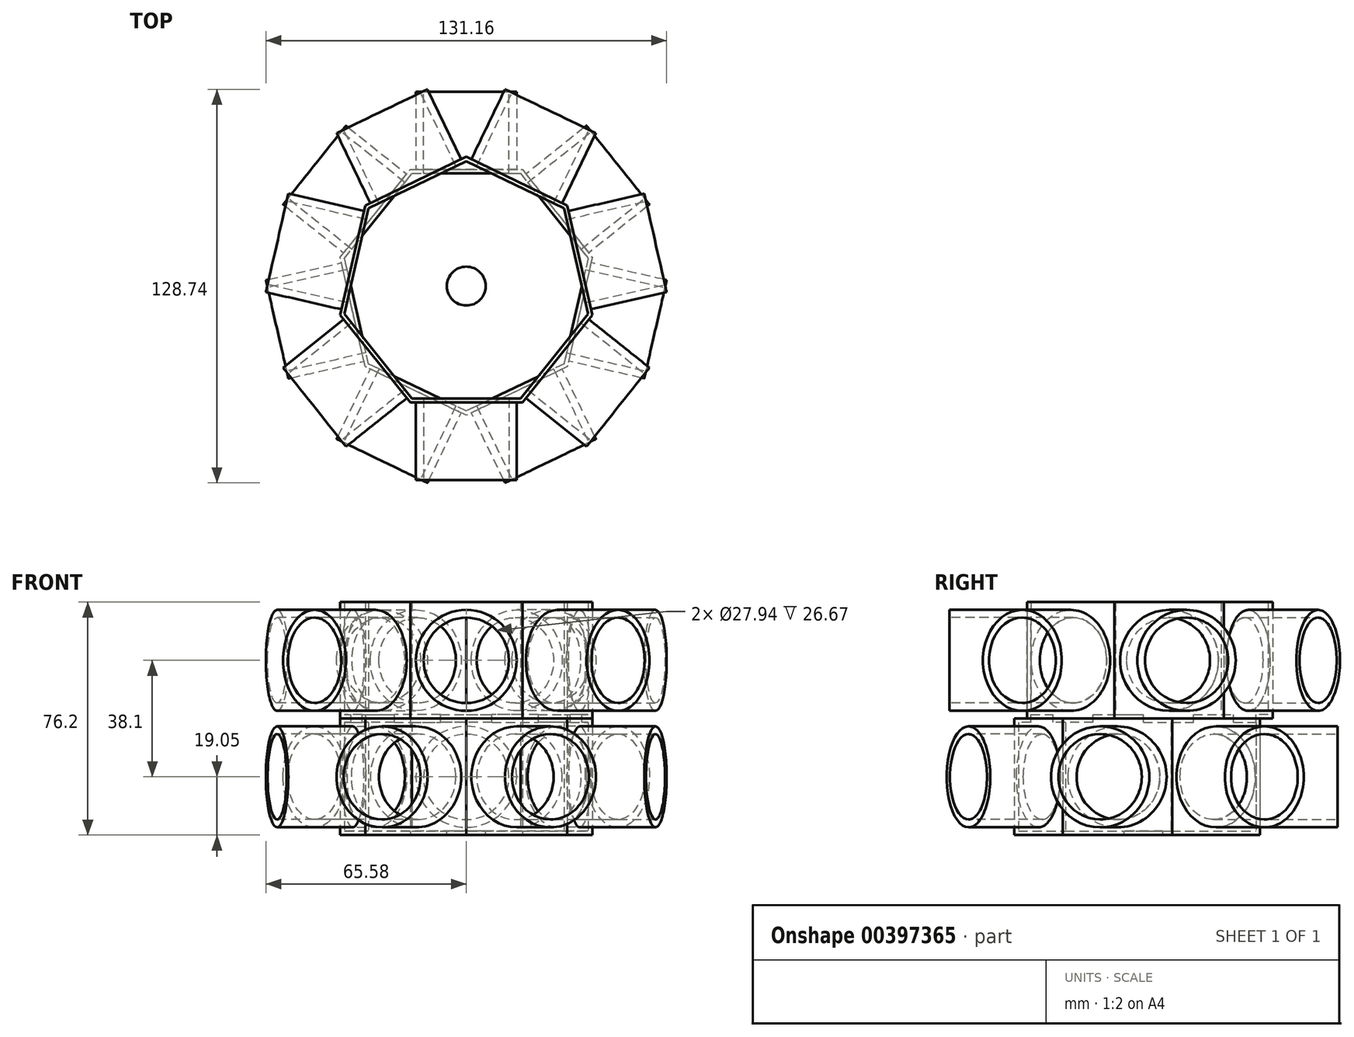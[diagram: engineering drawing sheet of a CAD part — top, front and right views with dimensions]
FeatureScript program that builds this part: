
annotation { "Feature Type Name" : "Feature", "Feature Type Description" : "" }
export const myFeature = defineFeature(function(context is Context, id is Id, definition is map)
    precondition{}
    {
        {
            var Q0;
            Q0=qCreatedBy(makeId("Top.planeOp"),FACE);
            var sketch = newSketch(context, id + "F0", { "sketchPlane" : qUnion([Q0])});
            skCircle(sketch, "E0.cCircle", {"center": v(0, 0) * mm, "radius": 38.1 * mm, "construction": true});
            skLineSegment(sketch, "E0.0", {"start": v(-18.35, 38.1) * mm, "end": v(18.35, 38.1) * mm});
            skLineSegment(sketch, "E0.1", {"start": v(18.35, 38.1) * mm, "end": v(41.23, 9.4) * mm});
            skLineSegment(sketch, "E0.2", {"start": v(41.23, 9.4) * mm, "end": v(33.06, -26.37) * mm});
            skLineSegment(sketch, "E0.3", {"start": v(33.06, -26.37) * mm, "end": v(0, -42.29) * mm});
            skLineSegment(sketch, "E0.4", {"start": v(0, -42.29) * mm, "end": v(-33.06, -26.37) * mm});
            skLineSegment(sketch, "E0.5", {"start": v(-33.06, -26.37) * mm, "end": v(-41.23, 9.4) * mm});
            skLineSegment(sketch, "E0.6", {"start": v(-41.23, 9.4) * mm, "end": v(-18.35, 38.1) * mm});
            skPoint(sketch, "E0.0.midPoint", {"position": v(0, 38.1) * mm});
            skSolve(sketch);
        }
        {
            var Q0;
            Q0=makeQuery(id+"F0.imprint","IMPRINT",FACE,{"disambiguationData":[TD([[makeQuery(id+"F0.imprint","IMPRINT",EDGE,{"derivedFrom":sQuery(id+"F0.wireOp",EDGE,"E0.0")}),-1.0]])]});
            extrude(context, id + "F1", {"entities" : qUnion([Q0]), "depth" : 38.1 * mm});
        }
        {
            var Q0;
            Q0=makeQuery(id+"F1.opExtrude","CAP_FACE",FACE,{"disambiguationData":[OSD([sQuery(id+"F0.wireOp",EDGE,"E0.0"),sQuery(id+"F0.wireOp",EDGE,"E0.1"),sQuery(id+"F0.wireOp",EDGE,"E0.2"),sQuery(id+"F0.wireOp",EDGE,"E0.3"),sQuery(id+"F0.wireOp",EDGE,"E0.4"),sQuery(id+"F0.wireOp",EDGE,"E0.5"),sQuery(id+"F0.wireOp",EDGE,"E0.6")])],"isStart":false});
            var sketch = newSketch(context, id + "F2", { "sketchPlane" : qUnion([Q0])});
            skCircle(sketch, "E1.cCircle", {"center": v(0, 0) * mm, "radius": 38.1 * mm, "construction": true});
            skLineSegment(sketch, "E1.0", {"start": v(0, 42.29) * mm, "end": v(33.06, 26.37) * mm});
            skLineSegment(sketch, "E1.1", {"start": v(33.06, 26.37) * mm, "end": v(41.23, -9.4) * mm});
            skLineSegment(sketch, "E1.2", {"start": v(41.23, -9.4) * mm, "end": v(18.35, -38.1) * mm});
            skLineSegment(sketch, "E1.3", {"start": v(18.35, -38.1) * mm, "end": v(-18.35, -38.1) * mm});
            skLineSegment(sketch, "E1.4", {"start": v(-18.35, -38.1) * mm, "end": v(-41.23, -9.4) * mm});
            skLineSegment(sketch, "E1.5", {"start": v(-41.23, -9.4) * mm, "end": v(-33.06, 26.37) * mm});
            skLineSegment(sketch, "E1.6", {"start": v(-33.06, 26.37) * mm, "end": v(0, 42.29) * mm});
            skPoint(sketch, "E1.0.midPoint", {"position": v(16.53, 34.33) * mm});
            skSolve(sketch);
        }
        {
            var Q0;
            {var subQ0=sQuery(id+"F2.wireOp",EDGE,"E1.6");var subQ1=sQuery(id+"F2.wireOp",EDGE,"E1.5");var subQ2=makeQuery(id+"F2.imprint","INTERSECT",VERTEX,{"derivedFrom":[subQ1,subQ0]});Q0=makeQuery(id+"F2.imprint","IMPRINT",FACE,{"disambiguationData":[TD([[makeQuery(id+"F2.imprint","IMPRINT",EDGE,{"disambiguationData":[TD([[subQ2,1.0]])],"derivedFrom":subQ1}),-1.0]])]});}
            var Q1;
            {var subQ0=sQuery(id+"F2.wireOp",EDGE,"E1.6");var subQ1=sQuery(id+"F2.wireOp",EDGE,"E1.0");var subQ2=makeQuery(id+"F2.imprint","INTERSECT",VERTEX,{"derivedFrom":[subQ1,subQ0]});Q1=makeQuery(id+"F2.imprint","IMPRINT",FACE,{"disambiguationData":[TD([[makeQuery(id+"F2.imprint","IMPRINT",EDGE,{"disambiguationData":[TD([[subQ2,-1.0]])],"derivedFrom":subQ1}),-1.0]])]});}
            var Q2;
            {var subQ0=sQuery(id+"F2.wireOp",EDGE,"E1.1");var subQ1=sQuery(id+"F2.wireOp",EDGE,"E1.0");var subQ2=makeQuery(id+"F2.imprint","INTERSECT",VERTEX,{"derivedFrom":[subQ1,subQ0]});Q2=makeQuery(id+"F2.imprint","IMPRINT",FACE,{"disambiguationData":[TD([[makeQuery(id+"F2.imprint","IMPRINT",EDGE,{"disambiguationData":[TD([[subQ2,1.0]])],"derivedFrom":subQ1}),-1.0]])]});}
            var Q3;
            {var subQ0=sQuery(id+"F2.wireOp",EDGE,"E1.2");var subQ1=sQuery(id+"F2.wireOp",EDGE,"E1.1");var subQ2=makeQuery(id+"F2.imprint","INTERSECT",VERTEX,{"derivedFrom":[subQ1,subQ0]});Q3=makeQuery(id+"F2.imprint","IMPRINT",FACE,{"disambiguationData":[TD([[makeQuery(id+"F2.imprint","IMPRINT",EDGE,{"disambiguationData":[TD([[subQ2,1.0]])],"derivedFrom":subQ1}),-1.0]])]});}
            var Q4;
            {var subQ0=sQuery(id+"F2.wireOp",EDGE,"E1.5");var subQ1=sQuery(id+"F2.wireOp",EDGE,"E1.4");var subQ2=makeQuery(id+"F2.imprint","INTERSECT",VERTEX,{"derivedFrom":[subQ1,subQ0]});Q4=makeQuery(id+"F2.imprint","IMPRINT",FACE,{"disambiguationData":[TD([[makeQuery(id+"F2.imprint","IMPRINT",EDGE,{"disambiguationData":[TD([[subQ2,1.0]])],"derivedFrom":subQ1}),-1.0]])]});}
            var Q5;
            {var subQ0=sQuery(id+"F2.wireOp",EDGE,"E1.4");var subQ1=sQuery(id+"F2.wireOp",EDGE,"E1.3");var subQ2=makeQuery(id+"F2.imprint","INTERSECT",VERTEX,{"derivedFrom":[subQ1,subQ0]});Q5=makeQuery(id+"F2.imprint","IMPRINT",FACE,{"disambiguationData":[TD([[makeQuery(id+"F2.imprint","IMPRINT",EDGE,{"disambiguationData":[TD([[subQ2,1.0]])],"derivedFrom":subQ1}),-1.0]])]});}
            var Q6;
            {var subQ0=sQuery(id+"F2.wireOp",EDGE,"E1.3");var subQ1=sQuery(id+"F2.wireOp",EDGE,"E1.2");var subQ2=makeQuery(id+"F2.imprint","INTERSECT",VERTEX,{"derivedFrom":[subQ1,subQ0]});Q6=makeQuery(id+"F2.imprint","IMPRINT",FACE,{"disambiguationData":[TD([[makeQuery(id+"F2.imprint","IMPRINT",EDGE,{"disambiguationData":[TD([[subQ2,1.0]])],"derivedFrom":subQ1}),-1.0]])]});}
            var Q7;
            {var subQ3=makeQuery(id+"F1.opExtrude","CAP_EDGE",EDGE,{"disambiguationData":[OSD([sQuery(id+"F0.wireOp",EDGE,"E0.0")])],"isStart":false});var subQ13=sQuery(id+"F2.wireOp",EDGE,"E1.0");var subQ14=makeQuery(id+"F2.imprint","INTERSECT",VERTEX,{"derivedFrom":[subQ3,subQ13]});Q7=makeQuery(id+"F2.imprint","IMPRINT",FACE,{"disambiguationData":[TD([[makeQuery(id+"F2.imprint","IMPRINT",EDGE,{"disambiguationData":[TD([[subQ14,-1.0]])],"derivedFrom":subQ13}),-1.0]])]});}
            extrude(context, id + "F3", {"entities" : qUnion([Q0, Q1, Q2, Q3, Q4, Q5, Q6, Q7]), "operationType" : NewBodyOperationType.ADD, "depth" : 38.1 * mm});
        }
        {
            var Q0;
            Q0=makeQuery(id+"F3.opExtrude","CAP_FACE",FACE,{"disambiguationData":[OSD([sQuery(id+"F2.wireOp",EDGE,"E1.0"),sQuery(id+"F2.wireOp",EDGE,"E1.1"),sQuery(id+"F2.wireOp",EDGE,"E1.2"),sQuery(id+"F2.wireOp",EDGE,"E1.3"),sQuery(id+"F2.wireOp",EDGE,"E1.4"),sQuery(id+"F2.wireOp",EDGE,"E1.5"),sQuery(id+"F2.wireOp",EDGE,"E1.6")])],"isStart":false});
            shell(context, id + "F4", {"entities" : qUnion([Q0]), "thickness" : 1.27 * mm});
        }
        {
            var Q0;
            Q0=makeQuery(id+"F1.opExtrude","CAP_FACE",FACE,{"disambiguationData":[OSD([sQuery(id+"F0.wireOp",EDGE,"E0.0"),sQuery(id+"F0.wireOp",EDGE,"E0.1"),sQuery(id+"F0.wireOp",EDGE,"E0.2"),sQuery(id+"F0.wireOp",EDGE,"E0.3"),sQuery(id+"F0.wireOp",EDGE,"E0.4"),sQuery(id+"F0.wireOp",EDGE,"E0.5"),sQuery(id+"F0.wireOp",EDGE,"E0.6")])],"isStart":true});
            var sketch = newSketch(context, id + "F5", { "sketchPlane" : qUnion([Q0])});
            skCircle(sketch, "E2", {"center": v(0, 0) * mm, "radius": 34.93 * mm});
            skSolve(sketch);
        }
        {
            var Q0;
            Q0=sQuery(id+"F5.wireOp",VERTEX,"E2.center");
            var Q1;
            Q1=makeQuery(id+"F1.opExtrude","SWEPT_BODY",BODY,{"disambiguationData":[OSD([sQuery(id+"F0.wireOp",EDGE,"E0.0"),sQuery(id+"F0.wireOp",EDGE,"E0.1"),sQuery(id+"F0.wireOp",EDGE,"E0.2"),sQuery(id+"F0.wireOp",EDGE,"E0.3"),sQuery(id+"F0.wireOp",EDGE,"E0.4"),sQuery(id+"F0.wireOp",EDGE,"E0.5"),sQuery(id+"F0.wireOp",EDGE,"E0.6")])]});
            hole(context, id + "F6", {"style" : HoleStyle.SIMPLE, "endStyle" : HoleEndStyle.THROUGH, "holeDiameter" : 12.7 * mm, "isTappedThrough" : true, "tappedDepth" : 12.7 * mm, "tapClearance" : 3, "startFromSketch" : true, "locations" : qUnion([Q0]), "scope" : qUnion([Q1])});
        }
        {
            var Q0;
            Q0=makeQuery(id+"F1.opExtrude","SWEPT_FACE",FACE,{"disambiguationData":[OSD([sQuery(id+"F0.wireOp",EDGE,"E0.0")])]});
            var sketch = newSketch(context, id + "F7", { "sketchPlane" : qUnion([Q0])});
            skCircle(sketch, "E3", {"center": v(0, 19.05) * mm, "radius": 13.97 * mm});
            skPoint(sketch, "E3.centerSnap0", {"position": v(18.35, 19.05) * mm});
            skCircle(sketch, "E4", {"center": v(0, 19.05) * mm, "radius": 16.51 * mm});
            skSolve(sketch);
        }
        {
            var Q0;
            Q0=makeQuery(id+"F7.imprint","IMPRINT",FACE,{"disambiguationData":[TD([[makeQuery(id+"F7.imprint","IMPRINT",EDGE,{"derivedFrom":sQuery(id+"F7.wireOp",EDGE,"E3")}),1.0]])]});
            extrude(context, id + "F8", {"entities" : qUnion([Q0]), "operationType" : NewBodyOperationType.REMOVE, "oppositeDirection" : true, "depth" : 25.4 * mm});
        }
        {
            var Q0;
            Q0=makeQuery(id+"F1.opExtrude","SWEPT_FACE",FACE,{"disambiguationData":[OSD([sQuery(id+"F0.wireOp",EDGE,"E0.1")])]});
            var sketch = newSketch(context, id + "F9", { "sketchPlane" : qUnion([Q0])});
            skCircle(sketch, "E5", {"center": v(0, 19.05) * mm, "radius": 13.97 * mm});
            skPoint(sketch, "E5.centerSnap0", {"position": v(-18.35, 19.05) * mm});
            skCircle(sketch, "E6", {"center": v(0, 19.05) * mm, "radius": 16.51 * mm});
            skSolve(sketch);
        }
        {
            var Q0;
            Q0=makeQuery(id+"F9.imprint","IMPRINT",FACE,{"disambiguationData":[TD([[makeQuery(id+"F9.imprint","IMPRINT",EDGE,{"derivedFrom":sQuery(id+"F9.wireOp",EDGE,"E5")}),1.0]])]});
            extrude(context, id + "F10", {"entities" : qUnion([Q0]), "operationType" : NewBodyOperationType.REMOVE, "oppositeDirection" : true, "depth" : 25.4 * mm});
        }
        {
            var Q0;
            Q0=makeQuery(id+"F1.opExtrude","SWEPT_FACE",FACE,{"disambiguationData":[OSD([sQuery(id+"F0.wireOp",EDGE,"E0.2")])]});
            var sketch = newSketch(context, id + "F11", { "sketchPlane" : qUnion([Q0])});
            skCircle(sketch, "E7", {"center": v(0, 19.05) * mm, "radius": 13.97 * mm});
            skPoint(sketch, "E7.centerSnap0", {"position": v(-18.35, 19.05) * mm});
            skCircle(sketch, "E8", {"center": v(0, 19.05) * mm, "radius": 16.51 * mm});
            skSolve(sketch);
        }
        {
            var Q0;
            Q0=makeQuery(id+"F11.imprint","IMPRINT",FACE,{"disambiguationData":[TD([[makeQuery(id+"F11.imprint","IMPRINT",EDGE,{"derivedFrom":sQuery(id+"F11.wireOp",EDGE,"E7")}),1.0]])]});
            extrude(context, id + "F12", {"entities" : qUnion([Q0]), "operationType" : NewBodyOperationType.REMOVE, "oppositeDirection" : true, "depth" : 25.4 * mm});
        }
        {
            var Q0;
            Q0=makeQuery(id+"F1.opExtrude","SWEPT_FACE",FACE,{"disambiguationData":[OSD([sQuery(id+"F0.wireOp",EDGE,"E0.3")])]});
            var sketch = newSketch(context, id + "F13", { "sketchPlane" : qUnion([Q0])});
            skCircle(sketch, "E9", {"center": v(0, 19.05) * mm, "radius": 13.97 * mm});
            skPoint(sketch, "E9.centerSnap0", {"position": v(18.35, 19.05) * mm});
            skCircle(sketch, "E10", {"center": v(0, 19.05) * mm, "radius": 16.51 * mm});
            skSolve(sketch);
        }
        {
            var Q0;
            Q0=makeQuery(id+"F13.imprint","IMPRINT",FACE,{"disambiguationData":[TD([[makeQuery(id+"F13.imprint","IMPRINT",EDGE,{"derivedFrom":sQuery(id+"F13.wireOp",EDGE,"E9")}),1.0]])]});
            extrude(context, id + "F14", {"entities" : qUnion([Q0]), "operationType" : NewBodyOperationType.REMOVE, "oppositeDirection" : true, "depth" : 25.4 * mm});
        }
        {
            var Q0;
            Q0=makeQuery(id+"F1.opExtrude","SWEPT_FACE",FACE,{"disambiguationData":[OSD([sQuery(id+"F0.wireOp",EDGE,"E0.5")])]});
            var sketch = newSketch(context, id + "F15", { "sketchPlane" : qUnion([Q0])});
            skCircle(sketch, "E11", {"center": v(0, 19.05) * mm, "radius": 13.97 * mm});
            skPoint(sketch, "E11.centerSnap0", {"position": v(18.35, 19.05) * mm});
            skCircle(sketch, "E12", {"center": v(0, 19.05) * mm, "radius": 16.51 * mm});
            skSolve(sketch);
        }
        {
            var Q0;
            Q0=makeQuery(id+"F15.imprint","IMPRINT",FACE,{"disambiguationData":[TD([[makeQuery(id+"F15.imprint","IMPRINT",EDGE,{"derivedFrom":sQuery(id+"F15.wireOp",EDGE,"E11")}),1.0]])]});
            extrude(context, id + "F16", {"entities" : qUnion([Q0]), "operationType" : NewBodyOperationType.REMOVE, "oppositeDirection" : true, "depth" : 25.4 * mm});
        }
        {
            var Q0;
            Q0=makeQuery(id+"F1.opExtrude","SWEPT_FACE",FACE,{"disambiguationData":[OSD([sQuery(id+"F0.wireOp",EDGE,"E0.4")])]});
            var sketch = newSketch(context, id + "F17", { "sketchPlane" : qUnion([Q0])});
            skCircle(sketch, "E13", {"center": v(0, 19.05) * mm, "radius": 13.97 * mm});
            skPoint(sketch, "E13.centerSnap0", {"position": v(18.35, 19.05) * mm});
            skCircle(sketch, "E14", {"center": v(0, 19.05) * mm, "radius": 16.51 * mm});
            skSolve(sketch);
        }
        {
            var Q0;
            Q0=makeQuery(id+"F17.imprint","IMPRINT",FACE,{"disambiguationData":[TD([[makeQuery(id+"F17.imprint","IMPRINT",EDGE,{"derivedFrom":sQuery(id+"F17.wireOp",EDGE,"E13")}),1.0]])]});
            extrude(context, id + "F18", {"entities" : qUnion([Q0]), "operationType" : NewBodyOperationType.REMOVE, "oppositeDirection" : true, "depth" : 25.4 * mm});
        }
        {
            var Q0;
            Q0=makeQuery(id+"F1.opExtrude","SWEPT_FACE",FACE,{"disambiguationData":[OSD([sQuery(id+"F0.wireOp",EDGE,"E0.6")])]});
            var sketch = newSketch(context, id + "F19", { "sketchPlane" : qUnion([Q0])});
            skCircle(sketch, "E15", {"center": v(0, 19.05) * mm, "radius": 13.97 * mm});
            skPoint(sketch, "E15.centerSnap0", {"position": v(18.35, 19.05) * mm});
            skCircle(sketch, "E16", {"center": v(0, 19.05) * mm, "radius": 16.51 * mm});
            skSolve(sketch);
        }
        {
            var Q0;
            Q0=makeQuery(id+"F19.imprint","IMPRINT",FACE,{"disambiguationData":[TD([[makeQuery(id+"F19.imprint","IMPRINT",EDGE,{"derivedFrom":sQuery(id+"F19.wireOp",EDGE,"E15")}),1.0]])]});
            extrude(context, id + "F20", {"entities" : qUnion([Q0]), "operationType" : NewBodyOperationType.REMOVE, "oppositeDirection" : true, "depth" : 25.4 * mm});
        }
        {
            var Q0;
            Q0=makeQuery(id+"F13.imprint","IMPRINT",FACE,{"disambiguationData":[TD([[makeQuery(id+"F13.imprint","IMPRINT",EDGE,{"derivedFrom":sQuery(id+"F13.wireOp",EDGE,"E9")}),-1.0]])]});
            extrude(context, id + "F21", {"entities" : qUnion([Q0]), "operationType" : NewBodyOperationType.ADD, "depth" : 25.4 * mm});
        }
        {
            var Q0;
            Q0=makeQuery(id+"F17.imprint","IMPRINT",FACE,{"disambiguationData":[TD([[makeQuery(id+"F17.imprint","IMPRINT",EDGE,{"derivedFrom":sQuery(id+"F17.wireOp",EDGE,"E13")}),-1.0]])]});
            extrude(context, id + "F22", {"entities" : qUnion([Q0]), "operationType" : NewBodyOperationType.ADD, "depth" : 25.4 * mm});
        }
        {
            var Q0;
            Q0=makeQuery(id+"F15.imprint","IMPRINT",FACE,{"disambiguationData":[TD([[makeQuery(id+"F15.imprint","IMPRINT",EDGE,{"derivedFrom":sQuery(id+"F15.wireOp",EDGE,"E11")}),-1.0]])]});
            extrude(context, id + "F23", {"entities" : qUnion([Q0]), "operationType" : NewBodyOperationType.ADD, "depth" : 25.4 * mm});
        }
        {
            var Q0;
            Q0=makeQuery(id+"F19.imprint","IMPRINT",FACE,{"disambiguationData":[TD([[makeQuery(id+"F19.imprint","IMPRINT",EDGE,{"derivedFrom":sQuery(id+"F19.wireOp",EDGE,"E15")}),-1.0]])]});
            extrude(context, id + "F24", {"entities" : qUnion([Q0]), "operationType" : NewBodyOperationType.ADD, "depth" : 25.4 * mm});
        }
        {
            var Q0;
            Q0=makeQuery(id+"F7.imprint","IMPRINT",FACE,{"disambiguationData":[TD([[makeQuery(id+"F7.imprint","IMPRINT",EDGE,{"derivedFrom":sQuery(id+"F7.wireOp",EDGE,"E3")}),-1.0]])]});
            extrude(context, id + "F25", {"entities" : qUnion([Q0]), "operationType" : NewBodyOperationType.ADD, "depth" : 25.4 * mm});
        }
        {
            var Q0;
            Q0=makeQuery(id+"F9.imprint","IMPRINT",FACE,{"disambiguationData":[TD([[makeQuery(id+"F9.imprint","IMPRINT",EDGE,{"derivedFrom":sQuery(id+"F9.wireOp",EDGE,"E5")}),-1.0]])]});
            extrude(context, id + "F26", {"entities" : qUnion([Q0]), "operationType" : NewBodyOperationType.ADD, "depth" : 25.4 * mm});
        }
        {
            var Q0;
            Q0=makeQuery(id+"F11.imprint","IMPRINT",FACE,{"disambiguationData":[TD([[makeQuery(id+"F11.imprint","IMPRINT",EDGE,{"derivedFrom":sQuery(id+"F11.wireOp",EDGE,"E7")}),-1.0]])]});
            extrude(context, id + "F27", {"entities" : qUnion([Q0]), "operationType" : NewBodyOperationType.ADD, "depth" : 25.4 * mm});
        }
        {
            var Q0;
            Q0=makeQuery(id+"F3.opExtrude","SWEPT_FACE",FACE,{"disambiguationData":[OSD([sQuery(id+"F2.wireOp",EDGE,"E1.3")])]});
            var sketch = newSketch(context, id + "F28", { "sketchPlane" : qUnion([Q0])});
            skCircle(sketch, "E17", {"center": v(0, 57.15) * mm, "radius": 16.51 * mm});
            skPoint(sketch, "E17.centerSnap0", {"position": v(0, 76.2) * mm});
            skPoint(sketch, "E17.centerSnap1", {"position": v(18.35, 57.15) * mm});
            skCircle(sketch, "E18", {"center": v(0, 57.15) * mm, "radius": 13.97 * mm});
            skSolve(sketch);
        }
        {
            var Q0;
            Q0=makeQuery(id+"F3.opExtrude","SWEPT_FACE",FACE,{"disambiguationData":[OSD([sQuery(id+"F2.wireOp",EDGE,"E1.2")])]});
            var sketch = newSketch(context, id + "F29", { "sketchPlane" : qUnion([Q0])});
            skCircle(sketch, "E19", {"center": v(0, 57.15) * mm, "radius": 13.97 * mm});
            skPoint(sketch, "E19.centerSnap0", {"position": v(-18.35, 57.15) * mm});
            skCircle(sketch, "E20", {"center": v(0, 57.15) * mm, "radius": 16.51 * mm});
            skSolve(sketch);
        }
        {
            var Q0;
            Q0=makeQuery(id+"F3.opExtrude","SWEPT_FACE",FACE,{"disambiguationData":[OSD([sQuery(id+"F2.wireOp",EDGE,"E1.1")])]});
            var sketch = newSketch(context, id + "F30", { "sketchPlane" : qUnion([Q0])});
            skCircle(sketch, "E21", {"center": v(0, 57.15) * mm, "radius": 13.97 * mm});
            skPoint(sketch, "E21.centerSnap0", {"position": v(18.35, 57.15) * mm});
            skPoint(sketch, "E21.centerSnap1", {"position": v(0, 76.2) * mm});
            skCircle(sketch, "E22", {"center": v(0, 57.15) * mm, "radius": 16.51 * mm});
            skSolve(sketch);
        }
        {
            var Q0;
            Q0=makeQuery(id+"F3.opExtrude","SWEPT_FACE",FACE,{"disambiguationData":[OSD([sQuery(id+"F2.wireOp",EDGE,"E1.0")])]});
            var sketch = newSketch(context, id + "F31", { "sketchPlane" : qUnion([Q0])});
            skCircle(sketch, "E23", {"center": v(0, 57.15) * mm, "radius": 16.51 * mm});
            skPoint(sketch, "E23.centerSnap0", {"position": v(0, 76.2) * mm});
            skPoint(sketch, "E23.centerSnap1", {"position": v(-18.35, 57.15) * mm});
            skCircle(sketch, "E24", {"center": v(0, 57.15) * mm, "radius": 13.97 * mm});
            skSolve(sketch);
        }
        {
            var Q0;
            Q0=makeQuery(id+"F3.opExtrude","SWEPT_FACE",FACE,{"disambiguationData":[OSD([sQuery(id+"F2.wireOp",EDGE,"E1.6")])]});
            var sketch = newSketch(context, id + "F32", { "sketchPlane" : qUnion([Q0])});
            skCircle(sketch, "E25", {"center": v(0, 57.15) * mm, "radius": 13.97 * mm});
            skPoint(sketch, "E25.centerSnap0", {"position": v(-18.35, 57.15) * mm});
            skCircle(sketch, "E26", {"center": v(0, 57.15) * mm, "radius": 16.51 * mm});
            skSolve(sketch);
        }
        {
            var Q0;
            Q0=makeQuery(id+"F3.opExtrude","SWEPT_FACE",FACE,{"disambiguationData":[OSD([sQuery(id+"F2.wireOp",EDGE,"E1.5")])]});
            var sketch = newSketch(context, id + "F33", { "sketchPlane" : qUnion([Q0])});
            skCircle(sketch, "E27", {"center": v(0, 57.15) * mm, "radius": 16.51 * mm});
            skPoint(sketch, "E27.centerSnap0", {"position": v(18.35, 57.15) * mm});
            skPoint(sketch, "E27.centerSnap1", {"position": v(0, 76.2) * mm});
            skCircle(sketch, "E28", {"center": v(0, 57.15) * mm, "radius": 13.97 * mm});
            skSolve(sketch);
        }
        {
            var Q0;
            Q0=makeQuery(id+"F33.imprint","IMPRINT",FACE,{"disambiguationData":[TD([[makeQuery(id+"F33.imprint","IMPRINT",EDGE,{"derivedFrom":sQuery(id+"F33.wireOp",EDGE,"E28")}),1.0]])]});
            extrude(context, id + "F34", {"entities" : qUnion([Q0]), "operationType" : NewBodyOperationType.REMOVE, "oppositeDirection" : true, "depth" : 25.4 * mm});
        }
        {
            var Q0;
            Q0=makeQuery(id+"F28.imprint","IMPRINT",FACE,{"disambiguationData":[TD([[makeQuery(id+"F28.imprint","IMPRINT",EDGE,{"derivedFrom":sQuery(id+"F28.wireOp",EDGE,"E18")}),1.0]])]});
            extrude(context, id + "F35", {"entities" : qUnion([Q0]), "operationType" : NewBodyOperationType.REMOVE, "oppositeDirection" : true, "depth" : 25.4 * mm});
        }
        {
            var Q0;
            Q0=makeQuery(id+"F29.imprint","IMPRINT",FACE,{"disambiguationData":[TD([[makeQuery(id+"F29.imprint","IMPRINT",EDGE,{"derivedFrom":sQuery(id+"F29.wireOp",EDGE,"E19")}),1.0]])]});
            extrude(context, id + "F36", {"entities" : qUnion([Q0]), "operationType" : NewBodyOperationType.REMOVE, "oppositeDirection" : true, "depth" : 25.4 * mm});
        }
        {
            var Q0;
            Q0=makeQuery(id+"F30.imprint","IMPRINT",FACE,{"disambiguationData":[TD([[makeQuery(id+"F30.imprint","IMPRINT",EDGE,{"derivedFrom":sQuery(id+"F30.wireOp",EDGE,"E21")}),1.0]])]});
            extrude(context, id + "F37", {"entities" : qUnion([Q0]), "operationType" : NewBodyOperationType.REMOVE, "oppositeDirection" : true, "depth" : 25.4 * mm});
        }
        {
            var Q0;
            Q0=makeQuery(id+"F31.imprint","IMPRINT",FACE,{"disambiguationData":[TD([[makeQuery(id+"F31.imprint","IMPRINT",EDGE,{"derivedFrom":sQuery(id+"F31.wireOp",EDGE,"E24")}),1.0]])]});
            extrude(context, id + "F38", {"entities" : qUnion([Q0]), "operationType" : NewBodyOperationType.REMOVE, "oppositeDirection" : true, "depth" : 25.4 * mm});
        }
        {
            var Q0;
            Q0=makeQuery(id+"F32.imprint","IMPRINT",FACE,{"disambiguationData":[TD([[makeQuery(id+"F32.imprint","IMPRINT",EDGE,{"derivedFrom":sQuery(id+"F32.wireOp",EDGE,"E25")}),1.0]])]});
            extrude(context, id + "F39", {"entities" : qUnion([Q0]), "operationType" : NewBodyOperationType.REMOVE, "oppositeDirection" : true, "depth" : 25.4 * mm});
        }
        {
            var Q0;
            Q0=makeQuery(id+"F3.opExtrude","SWEPT_FACE",FACE,{"disambiguationData":[OSD([sQuery(id+"F2.wireOp",EDGE,"E1.4")])]});
            var sketch = newSketch(context, id + "F40", { "sketchPlane" : qUnion([Q0])});
            skCircle(sketch, "E29", {"center": v(0, 57.15) * mm, "radius": 16.51 * mm});
            skPoint(sketch, "E29.centerSnap0", {"position": v(0, 76.2) * mm});
            skPoint(sketch, "E29.centerSnap1", {"position": v(-18.35, 57.15) * mm});
            skCircle(sketch, "E30", {"center": v(0, 57.15) * mm, "radius": 13.97 * mm});
            skSolve(sketch);
        }
        {
            var Q0;
            Q0=makeQuery(id+"F40.imprint","IMPRINT",FACE,{"disambiguationData":[TD([[makeQuery(id+"F40.imprint","IMPRINT",EDGE,{"derivedFrom":sQuery(id+"F40.wireOp",EDGE,"E30")}),1.0]])]});
            extrude(context, id + "F41", {"entities" : qUnion([Q0]), "operationType" : NewBodyOperationType.REMOVE, "oppositeDirection" : true, "depth" : 25.4 * mm});
        }
        {
            var Q0;
            Q0=makeQuery(id+"F33.imprint","IMPRINT",FACE,{"disambiguationData":[TD([[makeQuery(id+"F33.imprint","IMPRINT",EDGE,{"derivedFrom":sQuery(id+"F33.wireOp",EDGE,"E27")}),1.0]])]});
            extrude(context, id + "F42", {"entities" : qUnion([Q0]), "operationType" : NewBodyOperationType.ADD, "depth" : 25.4 * mm});
        }
        {
            var Q0;
            Q0=makeQuery(id+"F40.imprint","IMPRINT",FACE,{"disambiguationData":[TD([[makeQuery(id+"F40.imprint","IMPRINT",EDGE,{"derivedFrom":sQuery(id+"F40.wireOp",EDGE,"E29")}),1.0]])]});
            extrude(context, id + "F43", {"entities" : qUnion([Q0]), "operationType" : NewBodyOperationType.ADD, "depth" : 25.4 * mm});
        }
        {
            var Q0;
            Q0=makeQuery(id+"F28.imprint","IMPRINT",FACE,{"disambiguationData":[TD([[makeQuery(id+"F28.imprint","IMPRINT",EDGE,{"derivedFrom":sQuery(id+"F28.wireOp",EDGE,"E17")}),1.0]])]});
            extrude(context, id + "F44", {"entities" : qUnion([Q0]), "operationType" : NewBodyOperationType.ADD, "depth" : 25.4 * mm});
        }
        {
            var Q0;
            Q0=makeQuery(id+"F29.imprint","IMPRINT",FACE,{"disambiguationData":[TD([[makeQuery(id+"F29.imprint","IMPRINT",EDGE,{"derivedFrom":sQuery(id+"F29.wireOp",EDGE,"E19")}),-1.0]])]});
            extrude(context, id + "F45", {"entities" : qUnion([Q0]), "operationType" : NewBodyOperationType.ADD, "depth" : 25.4 * mm});
        }
        {
            var Q0;
            Q0=makeQuery(id+"F30.imprint","IMPRINT",FACE,{"disambiguationData":[TD([[makeQuery(id+"F30.imprint","IMPRINT",EDGE,{"derivedFrom":sQuery(id+"F30.wireOp",EDGE,"E21")}),-1.0]])]});
            extrude(context, id + "F46", {"entities" : qUnion([Q0]), "operationType" : NewBodyOperationType.ADD, "depth" : 25.4 * mm});
        }
        {
            var Q0;
            Q0=makeQuery(id+"F32.imprint","IMPRINT",FACE,{"disambiguationData":[TD([[makeQuery(id+"F32.imprint","IMPRINT",EDGE,{"derivedFrom":sQuery(id+"F32.wireOp",EDGE,"E25")}),-1.0]])]});
            extrude(context, id + "F47", {"entities" : qUnion([Q0]), "operationType" : NewBodyOperationType.ADD, "depth" : 25.4 * mm});
        }
        {
            var Q0;
            Q0=makeQuery(id+"F31.imprint","IMPRINT",FACE,{"disambiguationData":[TD([[makeQuery(id+"F31.imprint","IMPRINT",EDGE,{"derivedFrom":sQuery(id+"F31.wireOp",EDGE,"E23")}),1.0]])]});
            extrude(context, id + "F48", {"entities" : qUnion([Q0]), "operationType" : NewBodyOperationType.ADD, "depth" : 25.4 * mm});
        }
    });
